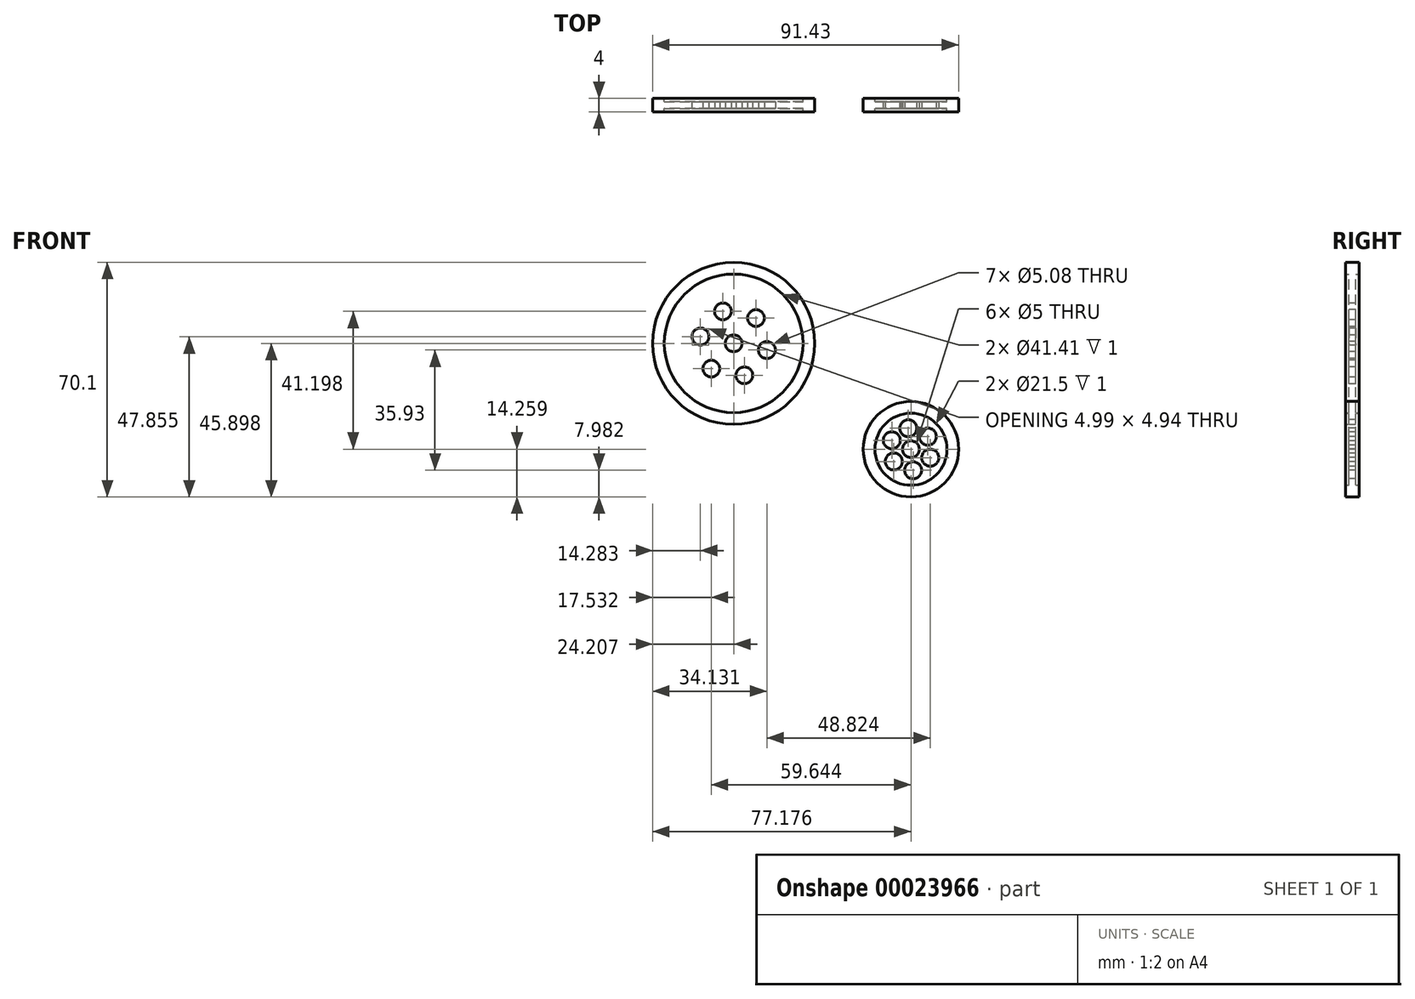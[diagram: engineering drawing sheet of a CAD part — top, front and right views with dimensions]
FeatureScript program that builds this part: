
annotation { "Feature Type Name" : "Feature", "Feature Type Description" : "" }
export const myFeature = defineFeature(function(context is Context, id is Id, definition is map)
    precondition{}
    {
        {
            var Q0;
            Q0=qCreatedBy(makeId("Front.planeOp"),FACE);
            var sketch = newSketch(context, id + "F0", { "sketchPlane" : qUnion([Q0])});
            skCircle(sketch, "E0", {"center": v(-45.74, 25.29) * mm, "radius": 20.7 * mm});
            skCircle(sketch, "E1", {"center": v(-45.74, 25.29) * mm, "radius": 24.2 * mm});
            skCircle(sketch, "E2", {"center": v(7.23, -6.35) * mm, "radius": 10.75 * mm});
            skCircle(sketch, "E3", {"center": v(7.23, -6.35) * mm, "radius": 14.26 * mm});
            skCircle(sketch, "E4", {"center": v(-45.74, 25.29) * mm, "radius": 2.5 * mm});
            skCircle(sketch, "E5", {"center": v(7.23, -6.35) * mm, "radius": 2.5 * mm});
            skPoint(sketch, "E6.center", {"position": v(0, 0) * mm});
            skCircle(sketch, "E7", {"center": v(-48.94, 34.85) * mm, "radius": 2.5 * mm});
            skCircle(sketch, "E8", {"center": v(-39.06, 32.84) * mm, "radius": 2.5 * mm});
            skCircle(sketch, "E9", {"center": v(-42.54, 15.73) * mm, "radius": 2.5 * mm});
            skCircle(sketch, "E10", {"center": v(-52.42, 17.73) * mm, "radius": 2.5 * mm});
            skCircle(sketch, "E11", {"center": v(-55.66, 27.31) * mm, "radius": 2.54 * mm});
            skCircle(sketch, "E12", {"center": v(-55.62, 27.3) * mm, "radius": 2.5 * mm});
            skCircle(sketch, "E13", {"center": v(-35.82, 23.3) * mm, "radius": 2.54 * mm});
            skCircle(sketch, "E14", {"center": v(1.5, -3.69) * mm, "radius": 2.54 * mm});
            skCircle(sketch, "E15", {"center": v(12.28, -2.58) * mm, "radius": 2.54 * mm});
            skCircle(sketch, "E16", {"center": v(7.87, -12.63) * mm, "radius": 2.54 * mm});
            skCircle(sketch, "E17", {"center": v(2.09, -10.01) * mm, "radius": 2.54 * mm});
            skCircle(sketch, "E18", {"center": v(13, -8.89) * mm, "radius": 2.54 * mm});
            skCircle(sketch, "E19", {"center": v(6.44, -0.09) * mm, "radius": 2.54 * mm});
            skSolve(sketch);
        }
        {
            var Q0;
            Q0 = qSketchRegion(id + "F0", true);
            extrude(context, id + "F1", {"entities" : qUnion([Q0]), "depth" : 2 * mm, "hasSecondDirection" : true, "secondDirectionOppositeDirection" : true, "secondDirectionDepth" : 2 * mm});
        }
        {
            var Q0;
            Q0=makeQuery(id+"F0.imprint","IMPRINT",FACE,{"disambiguationData":[TD([[makeQuery(id+"F0.imprint","IMPRINT",EDGE,{"derivedFrom":sQuery(id+"F0.wireOp",EDGE,"E0")}),1.0]])]});
            var Q1;
            Q1=makeQuery(id+"F0.imprint","IMPRINT",FACE,{"disambiguationData":[TD([[makeQuery(id+"F0.imprint","IMPRINT",EDGE,{"derivedFrom":sQuery(id+"F0.wireOp",EDGE,"E2")}),1.0]])]});
            extrude(context, id + "F2", {"entities" : qUnion([Q0, Q1]), "operationType" : NewBodyOperationType.ADD, "oppositeDirection" : true, "depth" : 1 * mm, "hasSecondDirection" : true, "secondDirectionOppositeDirection" : false, "secondDirectionDepth" : 1 * mm});
        }
    });
